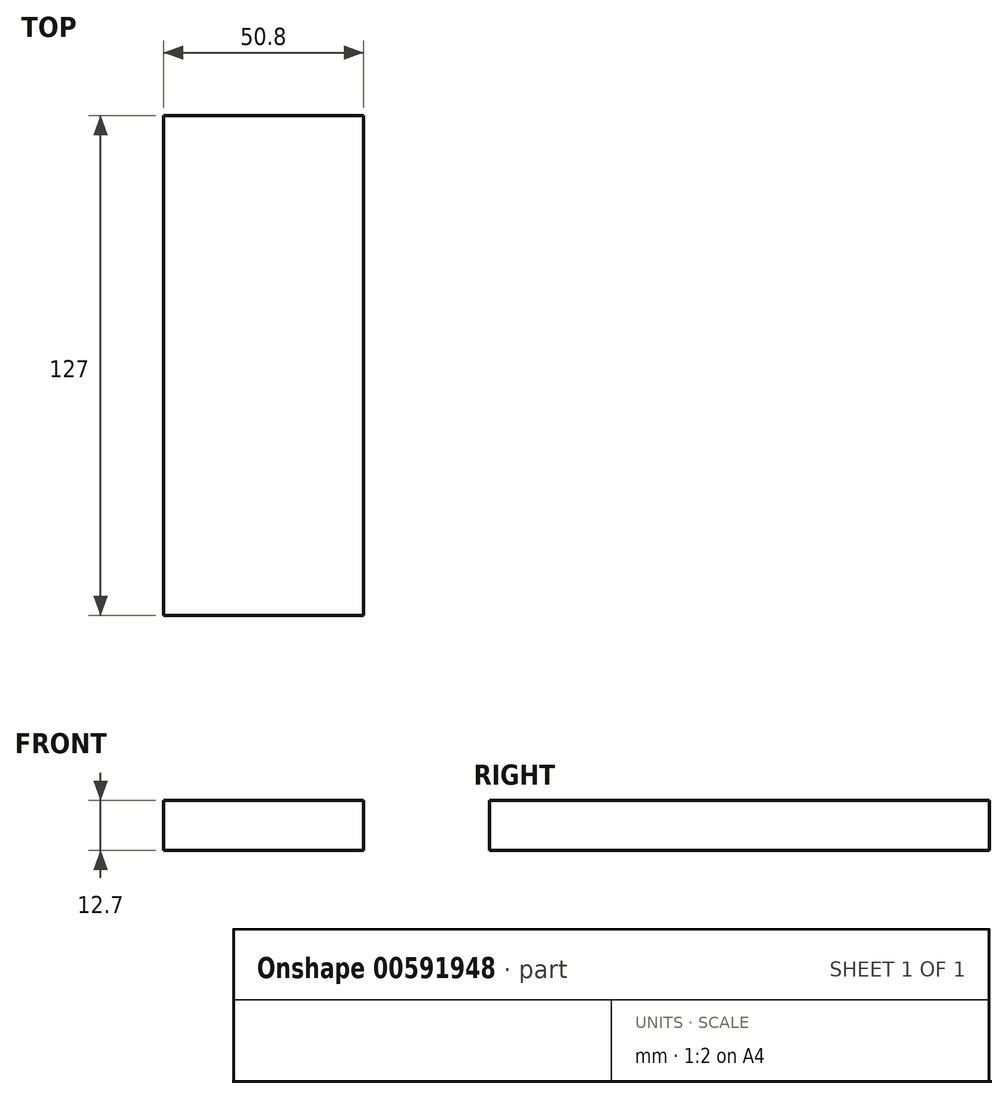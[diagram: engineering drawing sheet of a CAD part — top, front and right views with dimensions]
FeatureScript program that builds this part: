
annotation { "Feature Type Name" : "Feature", "Feature Type Description" : "" }
export const myFeature = defineFeature(function(context is Context, id is Id, definition is map)
    precondition{}
    {
        {
            var Q0;
            Q0=qCreatedBy(makeId("Front.planeOp"),FACE);
            var sketch = newSketch(context, id + "F0", { "sketchPlane" : qUnion([Q0])});
            skLineSegment(sketch, "E0.bottom", {"start": v(-71.18, -10.22) * mm, "end": v(-20.38, -10.22) * mm});
            skLineSegment(sketch, "E0.top", {"start": v(-71.18, 2.48) * mm, "end": v(-20.38, 2.48) * mm});
            skLineSegment(sketch, "E0.left", {"start": v(-71.18, -10.22) * mm, "end": v(-71.18, 2.48) * mm});
            skLineSegment(sketch, "E0.right", {"start": v(-20.38, -10.22) * mm, "end": v(-20.38, 2.48) * mm});
            skSolve(sketch);
        }
        {
            var Q0;
            Q0=makeQuery(id+"F0.imprint","IMPRINT",FACE,{"disambiguationData":[TD([[makeQuery(id+"F0.imprint","IMPRINT",EDGE,{"derivedFrom":sQuery(id+"F0.wireOp",EDGE,"E0.bottom")}),1.0]])]});
            extrude(context, id + "F1", {"entities" : qUnion([Q0]), "depth" : -127 * mm, "offsetDistance" : 25.4 * mm});
        }
    });
